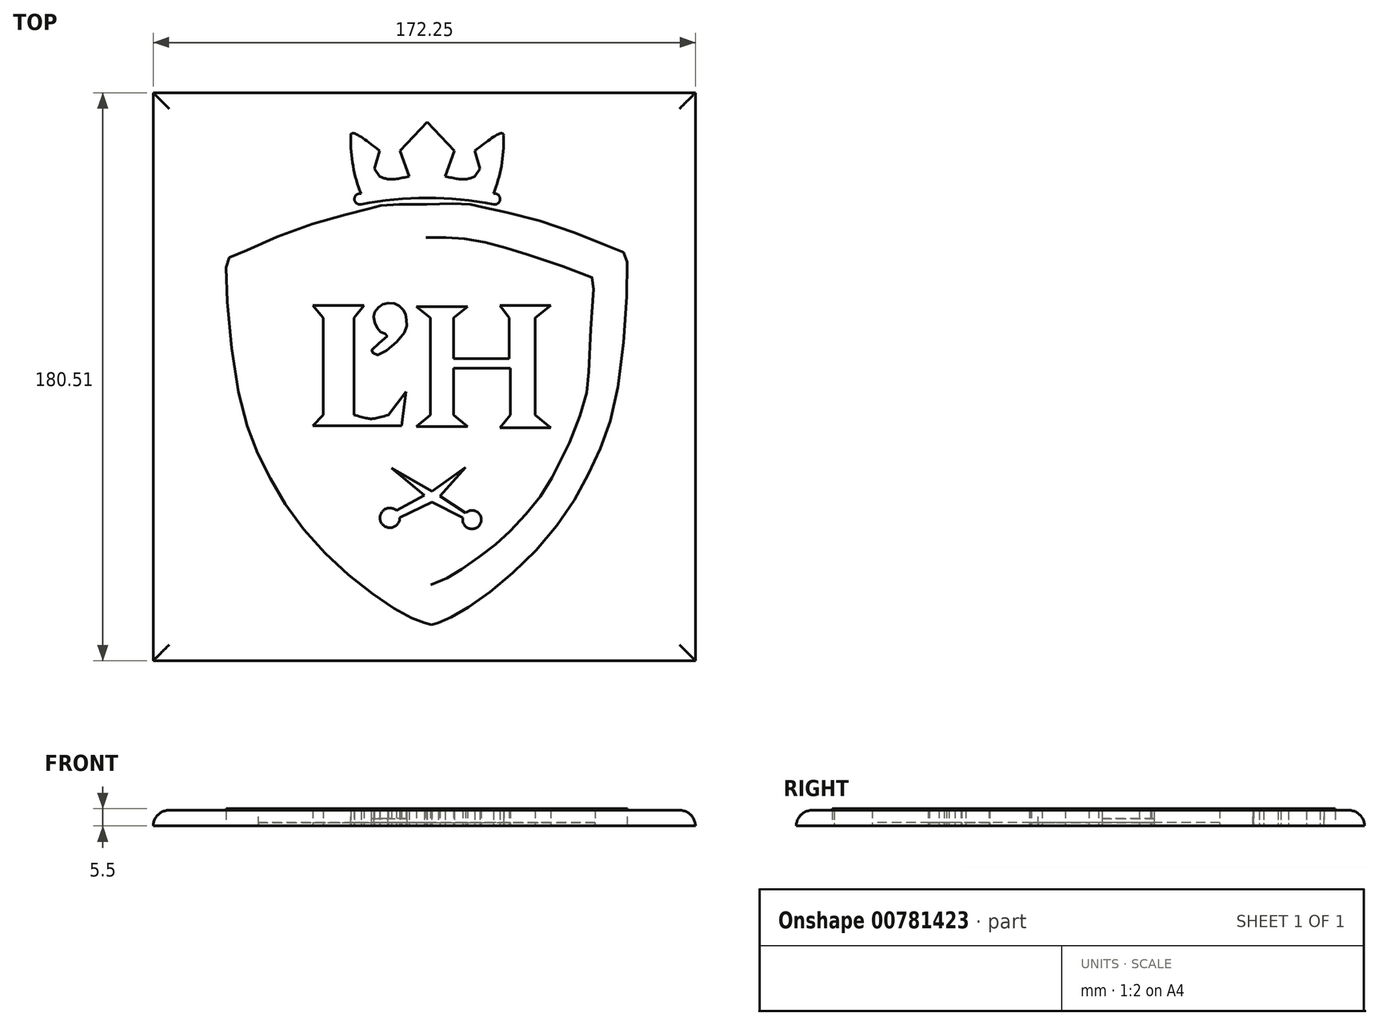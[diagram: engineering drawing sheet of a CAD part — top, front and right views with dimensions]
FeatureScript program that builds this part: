
annotation { "Feature Type Name" : "Feature", "Feature Type Description" : "" }
export const myFeature = defineFeature(function(context is Context, id is Id, definition is map)
    precondition{}
    {
        {
            var Q0;
            Q0=qCreatedBy(makeId("Top.planeOp"),FACE);
            var sketch = newSketch(context, id + "F0", { "sketchPlane" : qUnion([Q0])});
            skFitSpline(sketch, "E0", {"points": [v(0, 7.9) * mm, v(-5.2, 10.03) * mm, v(-18.93, 18.92) * mm, v(-38.45, 37.67) * mm, v(-51.2, 58.15) * mm, v(-59.7, 84.63) * mm, v(-62.8, 123.36) * mm, v(-61.82, 124) * mm, v(-41.35, 132.79) * mm, v(-17.3, 139.61) * mm, v(-13.4, 140.59) * mm, v(0, 140.91) * mm], "startDerivative": vector(-88.38, 30.93) * mm, "endDerivative": vector(194.4, -0.68) * mm});
            skLineSegment(sketch, "E1", {"start": v(0, 7.9) * mm, "end": v(2.2, 7.26) * mm});
            skFitSpline(sketch, "E2.MirrorCS", {"points": [v(4.4, 7.97) * mm, v(9.55, 10.23) * mm, v(23.02, 19.5) * mm, v(42.01, 38.77) * mm, v(54.2, 59.6) * mm, v(61.98, 86.3) * mm, v(64, 125.1) * mm, v(63.01, 125.72) * mm, v(42.3, 133.93) * mm, v(18.07, 140.1) * mm, v(14.15, 140.96) * mm, v(0.75, 140.92) * mm], "startDerivative": vector(87.5, 33.34) * mm, "endDerivative": vector(-194.3, -6) * mm});
            skLineSegment(sketch, "E3", {"start": v(4.4, 7.97) * mm, "end": v(2.2, 7.26) * mm});
            skFitSpline(sketch, "E4", {"points": [v(0.52, 130.42) * mm, v(-7.05, 130.1) * mm, v(-14.04, 129.3) * mm, v(-23.14, 126.86) * mm, v(-33.7, 123.28) * mm, v(-52.55, 115.8) * mm, v(-52.55, 114.66) * mm, v(-49.91, 85.82) * mm, v(-48.6, 78) * mm, v(-43.22, 63.81) * mm, v(-39.64, 57.46) * mm, v(-35.56, 49.96) * mm, v(-29.21, 42.13) * mm, v(-22.05, 34.95) * mm, v(-16.52, 30.55) * mm, v(-8.54, 25.16) * mm, v(-3.66, 22.23) * mm, v(2.03, 19.95) * mm], "startDerivative": vector(-146.42, -5.15) * mm, "endDerivative": vector(125.7, -45.31) * mm});
            skFitSpline(sketch, "E5.MirrorCS", {"points": [v(0.52, 130.42) * mm, v(8.09, 130.3) * mm, v(15.1, 129.7) * mm, v(24.26, 127.5) * mm, v(34.92, 124.22) * mm, v(53.97, 117.26) * mm, v(54, 116.12) * mm, v(52.15, 87.22) * mm, v(51.06, 79.36) * mm, v(46.07, 65.04) * mm, v(42.66, 58.58) * mm, v(38.8, 50.98) * mm, v(32.66, 42.98) * mm, v(25.7, 35.6) * mm, v(20.29, 31.05) * mm, v(12.46, 25.45) * mm, v(7.66, 22.38) * mm, v(2.03, 19.95) * mm], "startDerivative": vector(146.5, -1.13) * mm, "endDerivative": vector(-124.4, -48.74) * mm});
            skLineSegment(sketch, "E6", {"start": v(-2.6, 108.35) * mm, "end": v(13.62, 108.35) * mm});
            skLineSegment(sketch, "E7", {"start": v(-35.44, 108.74) * mm, "end": v(-19.21, 108.74) * mm});
            skLineSegment(sketch, "E8", {"start": v(-2.6, 70.3) * mm, "end": v(13.62, 70.3) * mm});
            skLineSegment(sketch, "E9", {"start": v(-2.6, 108.35) * mm, "end": v(1.84, 104.88) * mm});
            skLineSegment(sketch, "E10", {"start": v(1.84, 104.88) * mm, "end": v(1.84, 73.98) * mm});
            skLineSegment(sketch, "E11", {"start": v(1.84, 73.98) * mm, "end": v(-2.6, 70.3) * mm});
            skLineSegment(sketch, "E12", {"start": v(13.62, 108.35) * mm, "end": v(9.17, 104.88) * mm});
            skLineSegment(sketch, "E13", {"start": v(9.17, 73.98) * mm, "end": v(13.62, 70.3) * mm});
            skLineSegment(sketch, "E14", {"start": v(9.17, 104.88) * mm, "end": v(9.17, 91.94) * mm});
            skLineSegment(sketch, "E15", {"start": v(9.17, 91.94) * mm, "end": v(26.94, 91.94) * mm});
            skLineSegment(sketch, "E16", {"start": v(26.94, 91.94) * mm, "end": v(26.94, 104.88) * mm});
            skLineSegment(sketch, "E17", {"start": v(26.94, 104.88) * mm, "end": v(23.92, 108.74) * mm});
            skLineSegment(sketch, "E18", {"start": v(23.92, 108.74) * mm, "end": v(40.07, 108.74) * mm});
            skLineSegment(sketch, "E19", {"start": v(40.07, 108.74) * mm, "end": v(35.14, 104.88) * mm});
            skLineSegment(sketch, "E20", {"start": v(35.14, 104.88) * mm, "end": v(35.14, 73.98) * mm});
            skLineSegment(sketch, "E21", {"start": v(35.14, 73.98) * mm, "end": v(40.07, 69.9) * mm});
            skLineSegment(sketch, "E22", {"start": v(40.07, 69.9) * mm, "end": v(23.92, 69.9) * mm});
            skLineSegment(sketch, "E23", {"start": v(23.92, 69.9) * mm, "end": v(27.29, 73.98) * mm});
            skLineSegment(sketch, "E24", {"start": v(27.29, 73.98) * mm, "end": v(27.29, 88.85) * mm});
            skLineSegment(sketch, "E25", {"start": v(27.29, 88.85) * mm, "end": v(9.17, 88.85) * mm});
            skLineSegment(sketch, "E26", {"start": v(9.17, 88.85) * mm, "end": v(9.17, 73.98) * mm});
            skLineSegment(sketch, "E27", {"start": v(-19.21, 108.74) * mm, "end": v(-22.4, 104.88) * mm});
            skLineSegment(sketch, "E28", {"start": v(-22.4, 104.88) * mm, "end": v(-22.4, 73.98) * mm});
            skLineSegment(sketch, "E29", {"start": v(-35.44, 108.74) * mm, "end": v(-32.15, 104.88) * mm});
            skLineSegment(sketch, "E30", {"start": v(-32.15, 104.88) * mm, "end": v(-32.15, 73.98) * mm});
            skLineSegment(sketch, "E31", {"start": v(-32.15, 73.98) * mm, "end": v(-35.44, 70.5) * mm});
            skLineSegment(sketch, "E32", {"start": v(-35.44, 70.5) * mm, "end": v(-7.24, 70.5) * mm});
            skLineSegment(sketch, "E33", {"start": v(-7.24, 70.5) * mm, "end": v(-5.89, 81.32) * mm});
            skLineSegment(sketch, "E34", {"start": v(-5.89, 81.32) * mm, "end": v(-11.49, 73.98) * mm});
            skFitSpline(sketch, "E35", {"points": [v(-22.4, 73.98) * mm, v(-17.94, 72.87) * mm, v(-16.16, 72.81) * mm, v(-11.49, 73.98) * mm], "startDerivative": vector(13.44, -3.6) * mm, "endDerivative": vector(13.8, 3.9) * mm});
            skPoint(sketch, "E36.2.internal.snap0", {"position": v(-33.8, 106.8) * mm});
            skPoint(sketch, "E36.11.internal.snap0", {"position": v(9.17, 98.4) * mm});
            skFitSpline(sketch, "E37", {"points": [v(-11.48, 109.47) * mm, v(-13.84, 108.82) * mm, v(-15.46, 107.2) * mm, v(-16.2, 105.33) * mm, v(-15.54, 102.57) * mm, v(-14.4, 100.79) * mm, v(-12.46, 99.73) * mm, v(-11.73, 99.32) * mm, v(-16.84, 94.37) * mm, v(-16.44, 93.72) * mm, v(-14.73, 93.07) * mm, v(-6.53, 99.97) * mm, v(-5.64, 103.3) * mm, v(-6.04, 105.98) * mm, v(-7.1, 107.77) * mm, v(-8.88, 109.23) * mm, v(-11.48, 109.47) * mm]});
            skLineSegment(sketch, "E38", {"start": v(13, 57.35) * mm, "end": v(2.32, 49.78) * mm});
            skLineSegment(sketch, "E39", {"start": v(2.32, 49.78) * mm, "end": v(-10.42, 57.11) * mm});
            skLineSegment(sketch, "E40", {"start": v(-10.42, 57.11) * mm, "end": v(0, 48.42) * mm});
            skLineSegment(sketch, "E41", {"start": v(0, 48.42) * mm, "end": v(-8.96, 43.67) * mm});
            skLineSegment(sketch, "E42", {"start": v(13, 57.35) * mm, "end": v(4.85, 48.22) * mm});
            skLineSegment(sketch, "E43", {"start": v(4.85, 48.22) * mm, "end": v(13, 42.81) * mm});
            skArc(sketch, "E44", {"start": v(-8.96, 43.67) * mm, "mid": v(-13.85, 39.96) * mm, "end": v(-7.86, 41.28) * mm});
            skArc(sketch, "E45", {"start": v(12.17, 41.28) * mm, "mid": v(17.67, 39.29) * mm, "end": v(13, 42.81) * mm});
            skLineSegment(sketch, "E46", {"start": v(-7.86, 41.28) * mm, "end": v(2.32, 46.3) * mm});
            skLineSegment(sketch, "E47", {"start": v(2.32, 46.3) * mm, "end": v(12.17, 41.28) * mm});
            skArc(sketch, "E48", {"start": v(-20.14, 144.29) * mm, "mid": v(-22.28, 142.6) * mm, "end": v(-20.14, 140.92) * mm});
            skArc(sketch, "E49", {"start": v(-23.37, 162.2) * mm, "mid": v(-22.7, 153.07) * mm, "end": v(-20.14, 144.29) * mm});
            skFitSpline(sketch, "E50", {"points": [v(-23.37, 162.2) * mm, v(-23.37, 163.24) * mm, v(-22.45, 163.46) * mm, v(-14.3, 157.95) * mm], "startDerivative": vector(-1, 5.95) * mm, "endDerivative": vector(16.2, -12.64) * mm});
            skLineSegment(sketch, "E51", {"start": v(-14.3, 157.95) * mm, "end": v(-15.9, 152.21) * mm});
            skLineSegment(sketch, "E52", {"start": v(-15.9, 152.21) * mm, "end": v(-14.3, 149.8) * mm});
            skFitSpline(sketch, "E53", {"points": [v(-14.3, 149.8) * mm, v(-11.08, 148.88) * mm, v(-4.88, 149.8) * mm], "startDerivative": vector(6.96, -2.97) * mm, "endDerivative": vector(11.63, 2.68) * mm});
            skLineSegment(sketch, "E54", {"start": v(-4.88, 149.8) * mm, "end": v(-7.75, 157.95) * mm});
            skLineSegment(sketch, "E55", {"start": v(-7.75, 157.95) * mm, "end": v(0.86, 167.02) * mm});
            skLineSegment(sketch, "E56.MirrorCS", {"start": v(9.48, 157.95) * mm, "end": v(0.86, 167.02) * mm});
            skLineSegment(sketch, "E57.MirrorCS", {"start": v(6.6, 149.8) * mm, "end": v(9.48, 157.95) * mm});
            skFitSpline(sketch, "E58.MirrorCS", {"points": [v(16.02, 149.8) * mm, v(12.8, 148.88) * mm, v(6.6, 149.8) * mm], "startDerivative": vector(-6.96, -2.97) * mm, "endDerivative": vector(-11.63, 2.68) * mm});
            skLineSegment(sketch, "E59.MirrorCS", {"start": v(17.63, 152.21) * mm, "end": v(16.02, 149.8) * mm});
            skLineSegment(sketch, "E60.MirrorCS", {"start": v(16.02, 157.95) * mm, "end": v(17.63, 152.21) * mm});
            skFitSpline(sketch, "E61.MirrorCS", {"points": [v(25.1, 162.2) * mm, v(25.1, 163.24) * mm, v(24.18, 163.46) * mm, v(16.02, 157.95) * mm], "startDerivative": vector(1, 5.95) * mm, "endDerivative": vector(-16.2, -12.64) * mm});
            skArc(sketch, "E62.MirrorCS", {"start": v(25.1, 162.2) * mm, "mid": v(24.44, 153.07) * mm, "end": v(21.87, 144.29) * mm});
            skArc(sketch, "E63.MirrorCS", {"start": v(21.87, 144.29) * mm, "mid": v(24, 142.6) * mm, "end": v(21.87, 140.92) * mm});
            skLineSegment(sketch, "E64", {"start": v(0.75, 140.92) * mm, "end": v(0, 140.91) * mm});
            skArc(sketch, "E65", {"start": v(21.87, 140.92) * mm, "mid": v(0.86, 142.98) * mm, "end": v(-20.14, 140.92) * mm});
            skLineSegment(sketch, "E66.bottom", {"start": v(-86.19, 176.38) * mm, "end": v(86.06, 176.38) * mm});
            skLineSegment(sketch, "E66.top", {"start": v(-86.19, -4.13) * mm, "end": v(86.06, -4.13) * mm});
            skLineSegment(sketch, "E66.left", {"start": v(-86.19, 176.38) * mm, "end": v(-86.19, -4.13) * mm});
            skLineSegment(sketch, "E66.right", {"start": v(86.06, 176.38) * mm, "end": v(86.06, -4.13) * mm});
            skLineSegment(sketch, "E67.left", {"start": v(86.06, 118.97) * mm, "end": v(86.52, 120.8) * mm});
            skSolve(sketch);
        }
        {
            var Q0;
            Q0=makeQuery(id+"F0.imprint","IMPRINT",FACE,{"disambiguationData":[TD([[makeQuery(id+"F0.imprint","IMPRINT",EDGE,{"derivedFrom":sQuery(id+"F0.wireOp",EDGE,"E48")}),1.0]])]});
            extrude(context, id + "F1", {"entities" : qUnion([Q0]), "depth" : 5.5 * mm, "offsetDistance" : 25.4 * mm});
        }
        {
            var Q0;
            Q0=makeQuery(id+"F0.imprint","IMPRINT",FACE,{"disambiguationData":[TD([[makeQuery(id+"F0.imprint","IMPRINT",EDGE,{"derivedFrom":sQuery(id+"F0.wireOp",EDGE,"E0")}),-1.0]])]});
            extrude(context, id + "F2", {"entities" : qUnion([Q0]), "depth" : 5.5 * mm, "offsetDistance" : 25.4 * mm});
        }
        {
            var Q0;
            Q0=makeQuery(id+"F0.imprint","IMPRINT",FACE,{"disambiguationData":[TD([[makeQuery(id+"F0.imprint","IMPRINT",EDGE,{"derivedFrom":sQuery(id+"F0.wireOp",EDGE,"E37")}),1.0]])]});
            extrude(context, id + "F3", {"entities" : qUnion([Q0]), "depth" : 2.3 * mm, "offsetDistance" : 25.4 * mm});
        }
        {
            var Q0;
            Q0=makeQuery(id+"F0.imprint","IMPRINT",FACE,{"disambiguationData":[TD([[makeQuery(id+"F0.imprint","IMPRINT",EDGE,{"derivedFrom":sQuery(id+"F0.wireOp",EDGE,"E6")}),-1.0]])]});
            extrude(context, id + "F4", {"entities" : qUnion([Q0]), "depth" : 5.5 * mm, "offsetDistance" : 25.4 * mm});
        }
        {
            var Q0;
            Q0=makeQuery(id+"F0.imprint","IMPRINT",FACE,{"disambiguationData":[TD([[makeQuery(id+"F0.imprint","IMPRINT",EDGE,{"derivedFrom":sQuery(id+"F0.wireOp",EDGE,"E38")}),1.0]])]});
            extrude(context, id + "F5", {"entities" : qUnion([Q0]), "depth" : 5.5 * mm, "offsetDistance" : 25.4 * mm});
        }
        {
            var Q0;
            Q0=makeQuery(id+"F0.imprint","IMPRINT",FACE,{"disambiguationData":[TD([[makeQuery(id+"F0.imprint","IMPRINT",EDGE,{"derivedFrom":sQuery(id+"F0.wireOp",EDGE,"E4")}),1.0]])]});
            extrude(context, id + "F6", {"entities" : qUnion([Q0]), "depth" : 1.02 * mm, "offsetDistance" : 25.4 * mm});
        }
        {
            var Q0;
            Q0=makeQuery(id+"F0.imprint","IMPRINT",FACE,{"disambiguationData":[TD([[makeQuery(id+"F0.imprint","IMPRINT",EDGE,{"derivedFrom":sQuery(id+"F0.wireOp",EDGE,"E0")}),1.0]])]});
            extrude(context, id + "F7", {"entities" : qUnion([Q0]), "depth" : 5 * mm, "offsetDistance" : 25.4 * mm});
        }
        {
            var Q0;
            Q0=makeQuery(id+"F7.opExtrude","CAP_EDGE",EDGE,{"disambiguationData":[OSD([sQuery(id+"F0.wireOp",EDGE,"E66.bottom")])],"isStart":false});
            var Q1;
            Q1=makeQuery(id+"F7.opExtrude","CAP_EDGE",EDGE,{"disambiguationData":[OSD([sQuery(id+"F0.wireOp",EDGE,"E66.top")])],"isStart":false});
            var Q2;
            Q2=makeQuery(id+"F7.opExtrude","CAP_EDGE",EDGE,{"disambiguationData":[OSD([sQuery(id+"F0.wireOp",EDGE,"E66.left")])],"isStart":false});
            var Q3;
            Q3=makeQuery(id+"F7.opExtrude","CAP_EDGE",EDGE,{"disambiguationData":[OSD([sQuery(id+"F0.wireOp",EDGE,"E66.right")])],"isStart":false});
            fillet(context, id + "F8", {"entities" : qUnion([Q0, Q1, Q2, Q3]), "radius" : 5.08 * mm, "tangentPropagation" : true, "allowEdgeOverflow" : false});
        }
        {
            var Q0;
            Q0=makeQuery(id+"F0.imprint","IMPRINT",FACE,{"disambiguationData":[TD([[makeQuery(id+"F0.imprint","IMPRINT",EDGE,{"derivedFrom":sQuery(id+"F0.wireOp",EDGE,"E7")}),-1.0]])]});
            var Q1;
            Q1=makeQuery(id+"F0.imprint","IMPRINT",FACE,{"disambiguationData":[TD([[makeQuery(id+"F0.imprint","IMPRINT",EDGE,{"derivedFrom":sQuery(id+"F0.wireOp",EDGE,"E37")}),1.0]])]});
            extrude(context, id + "F9", {"entities" : qUnion([Q0, Q1]), "depth" : 5.5 * mm, "offsetDistance" : 25.4 * mm});
        }
    });
